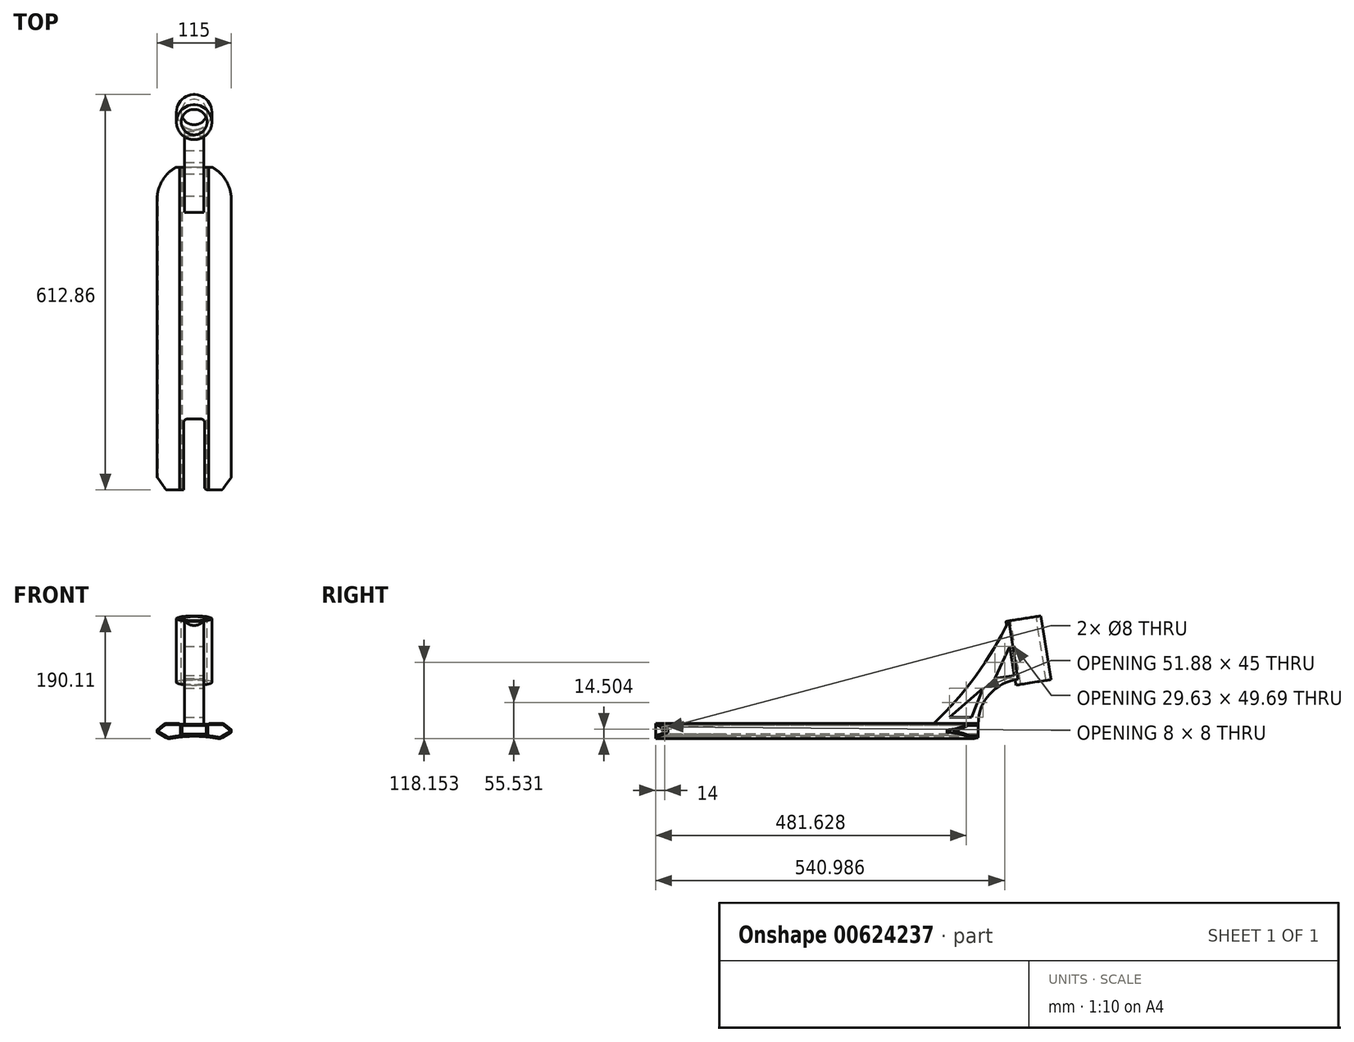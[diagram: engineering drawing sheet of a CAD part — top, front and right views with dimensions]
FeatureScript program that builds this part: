
annotation { "Feature Type Name" : "Feature", "Feature Type Description" : "" }
export const myFeature = defineFeature(function(context is Context, id is Id, definition is map)
    precondition{}
    {
        {
            var Q0;
            Q0=qCreatedBy(makeId("Front.planeOp"),FACE);
            var sketch = newSketch(context, id + "F0", { "sketchPlane" : qUnion([Q0])});
            skLineSegment(sketch, "E0", {"start": v(0, 0) * mm, "end": v(0, 27.74) * mm, "construction": true});
            skLineSegment(sketch, "E1", {"start": v(0, 23.15) * mm, "end": v(22.5, 23.15) * mm});
            skLineSegment(sketch, "E2", {"start": v(22.5, 23.15) * mm, "end": v(22.5, 24.45) * mm});
            skLineSegment(sketch, "E3", {"start": v(22.5, 24.45) * mm, "end": v(45.58, 24.45) * mm});
            skLineSegment(sketch, "E4", {"start": v(45.58, 24.45) * mm, "end": v(57.5, 14.45) * mm});
            skLineSegment(sketch, "E5", {"start": v(57.5, 14.45) * mm, "end": v(57.5, 10.45) * mm});
            skLineSegment(sketch, "E6", {"start": v(57.5, 10.45) * mm, "end": v(40.18, 0.45) * mm});
            skLineSegment(sketch, "E7.MirrorCS", {"start": v(0, 23.15) * mm, "end": v(-22.5, 23.15) * mm});
            skLineSegment(sketch, "E8.MirrorCS", {"start": v(-22.5, 23.15) * mm, "end": v(-22.5, 24.45) * mm});
            skLineSegment(sketch, "E9.MirrorCS", {"start": v(-22.5, 24.45) * mm, "end": v(-45.58, 24.45) * mm});
            skLineSegment(sketch, "E10.MirrorCS", {"start": v(-45.58, 24.45) * mm, "end": v(-57.5, 14.45) * mm});
            skLineSegment(sketch, "E11.MirrorCS", {"start": v(-57.5, 14.45) * mm, "end": v(-57.5, 10.45) * mm});
            skLineSegment(sketch, "E12.MirrorCS", {"start": v(-57.5, 10.45) * mm, "end": v(-40.18, 0.45) * mm});
            skArc(sketch, "E13", {"start": v(40.18, 0.45) * mm, "mid": v(0, 4.53) * mm, "end": v(-40.18, 0.45) * mm});
            skSolve(sketch);
        }
        {
            var Q0;
            Q0=qSketchRegion(id+"F0",true);
            extrude(context, id + "F1", {"entities" : qUnion([Q0]), "endBound" : BoundingType.SYMMETRIC, "depth" : 500 * mm});
        }
        {
            var Q0;
            Q0=qCreatedBy(makeId("Front.planeOp"),FACE);
            var sketch = newSketch(context, id + "F2", { "sketchPlane" : qUnion([Q0])});
            skLineSegment(sketch, "E14.bottom", {"start": v(-19, 21.15) * mm, "end": v(19, 21.15) * mm});
            skLineSegment(sketch, "E14.top", {"start": v(-19, 8.15) * mm, "end": v(19, 8.15) * mm});
            skLineSegment(sketch, "E14.left", {"start": v(-19, 21.15) * mm, "end": v(-19, 8.15) * mm});
            skLineSegment(sketch, "E14.right", {"start": v(19, 21.15) * mm, "end": v(19, 8.15) * mm});
            skSolve(sketch);
        }
        {
            var Q0;
            Q0=qSketchRegion(id+"F2",true);
            extrude(context, id + "F3", {"entities" : qUnion([Q0]), "operationType" : NewBodyOperationType.REMOVE, "endBound" : BoundingType.SYMMETRIC, "oppositeDirection" : true, "depth" : 500 * mm});
        }
        {
            var Q0;
            Q0=makeQuery(id+"F1.opExtrude","SWEPT_EDGE",EDGE,{"disambiguationData":[OSD([sQuery(id+"F0.wireOp",EDGE,"E8.MirrorCS"),sQuery(id+"F0.wireOp",EDGE,"E9.MirrorCS")])]});
            var Q1;
            Q1=makeQuery(id+"F1.opExtrude","SWEPT_EDGE",EDGE,{"disambiguationData":[OSD([sQuery(id+"F0.wireOp",EDGE,"E2"),sQuery(id+"F0.wireOp",EDGE,"E3")])]});
            fillet(context, id + "F4", {"entities" : qUnion([Q0, Q1]), "radius" : 2 * mm, "tangentPropagation" : true, "allowEdgeOverflow" : false});
        }
        {
            var Q0;
            Q0=makeQuery(id+"F1.opExtrude","SWEPT_EDGE",EDGE,{"disambiguationData":[OSD([sQuery(id+"F0.wireOp",EDGE,"E9.MirrorCS"),sQuery(id+"F0.wireOp",EDGE,"E10.MirrorCS")])]});
            var Q1;
            Q1=makeQuery(id+"F1.opExtrude","SWEPT_EDGE",EDGE,{"disambiguationData":[OSD([sQuery(id+"F0.wireOp",EDGE,"E12.MirrorCS"),sQuery(id+"F0.wireOp",EDGE,"E13")])]});
            var Q2;
            Q2=makeQuery(id+"F1.opExtrude","SWEPT_EDGE",EDGE,{"disambiguationData":[OSD([sQuery(id+"F0.wireOp",EDGE,"E6"),sQuery(id+"F0.wireOp",EDGE,"E13")])]});
            var Q3;
            Q3=makeQuery(id+"F1.opExtrude","SWEPT_EDGE",EDGE,{"disambiguationData":[OSD([sQuery(id+"F0.wireOp",EDGE,"E3"),sQuery(id+"F0.wireOp",EDGE,"E4")])]});
            fillet(context, id + "F5", {"entities" : qUnion([Q0, Q1, Q2, Q3]), "radius" : 9 * mm, "tangentPropagation" : true, "allowEdgeOverflow" : false});
        }
        {
            var Q0;
            Q0=makeQuery(id+"F1.opExtrude","SWEPT_EDGE",EDGE,{"disambiguationData":[OSD([sQuery(id+"F0.wireOp",EDGE,"E4"),sQuery(id+"F0.wireOp",EDGE,"E5")])]});
            var Q1;
            Q1=makeQuery(id+"F1.opExtrude","SWEPT_EDGE",EDGE,{"disambiguationData":[OSD([sQuery(id+"F0.wireOp",EDGE,"E5"),sQuery(id+"F0.wireOp",EDGE,"E6")])]});
            var Q2;
            Q2=makeQuery(id+"F1.opExtrude","SWEPT_EDGE",EDGE,{"disambiguationData":[OSD([sQuery(id+"F0.wireOp",EDGE,"E11.MirrorCS"),sQuery(id+"F0.wireOp",EDGE,"E12.MirrorCS")])]});
            var Q3;
            Q3=makeQuery(id+"F1.opExtrude","SWEPT_EDGE",EDGE,{"disambiguationData":[OSD([sQuery(id+"F0.wireOp",EDGE,"E10.MirrorCS"),sQuery(id+"F0.wireOp",EDGE,"E11.MirrorCS")])]});
            fillet(context, id + "F6", {"entities" : qUnion([Q0, Q1, Q2, Q3]), "radius" : 1 * mm, "tangentPropagation" : true, "allowEdgeOverflow" : false});
        }
        {
            var Q0;
            Q0=makeQuery(id+"F1.opExtrude","CAP_FACE",FACE,{"disambiguationData":[OSD([sQuery(id+"F0.wireOp",EDGE,"E1"),sQuery(id+"F0.wireOp",EDGE,"E2"),sQuery(id+"F0.wireOp",EDGE,"E3"),sQuery(id+"F0.wireOp",EDGE,"E4"),sQuery(id+"F0.wireOp",EDGE,"E5"),sQuery(id+"F0.wireOp",EDGE,"E6"),sQuery(id+"F0.wireOp",EDGE,"E7.MirrorCS"),sQuery(id+"F0.wireOp",EDGE,"E8.MirrorCS"),sQuery(id+"F0.wireOp",EDGE,"E9.MirrorCS"),sQuery(id+"F0.wireOp",EDGE,"E10.MirrorCS"),sQuery(id+"F0.wireOp",EDGE,"E11.MirrorCS"),sQuery(id+"F0.wireOp",EDGE,"E12.MirrorCS"),sQuery(id+"F0.wireOp",EDGE,"E13")])],"isStart":false});
            var sketch = newSketch(context, id + "F7", { "sketchPlane" : qUnion([Q0])});
            skLineSegment(sketch, "E15.0.0", {"start": v(43.1, 2.14) * mm, "end": v(57, 10.16) * mm});
            skArc(sketch, "E15.0.1", {"start": v(57, 10.16) * mm, "mid": v(57.37, 10.53) * mm, "end": v(57.5, 11.03) * mm});
            skLineSegment(sketch, "E15.0.2", {"start": v(57.5, 11.03) * mm, "end": v(57.5, 13.99) * mm});
            skArc(sketch, "E15.0.3", {"start": v(57.5, 13.99) * mm, "mid": v(57.4, 14.4) * mm, "end": v(57.14, 14.75) * mm});
            skLineSegment(sketch, "E15.0.4", {"start": v(57.14, 14.75) * mm, "end": v(48.1, 22.35) * mm});
            skArc(sketch, "E15.0.5", {"start": v(48.1, 22.35) * mm, "mid": v(45.38, 23.9) * mm, "end": v(42.3, 24.45) * mm});
            skLineSegment(sketch, "E15.0.6", {"start": v(42.3, 24.45) * mm, "end": v(24.37, 24.45) * mm});
            skArc(sketch, "E15.0.7", {"start": v(24.37, 24.45) * mm, "mid": v(23.23, 24.1) * mm, "end": v(22.5, 23.15) * mm});
            skLineSegment(sketch, "E15.0.8", {"start": v(22.5, 23.15) * mm, "end": v(-22.5, 23.15) * mm});
            skArc(sketch, "E15.0.9", {"start": v(-22.5, 23.15) * mm, "mid": v(-23.23, 24.1) * mm, "end": v(-24.37, 24.45) * mm});
            skLineSegment(sketch, "E15.0.10", {"start": v(-24.37, 24.45) * mm, "end": v(-42.3, 24.45) * mm});
            skArc(sketch, "E15.0.11", {"start": v(-42.3, 24.45) * mm, "mid": v(-45.38, 23.9) * mm, "end": v(-48.1, 22.35) * mm});
            skLineSegment(sketch, "E15.0.12", {"start": v(-48.1, 22.35) * mm, "end": v(-57.14, 14.75) * mm});
            skArc(sketch, "E15.0.13", {"start": v(-57.14, 14.75) * mm, "mid": v(-57.4, 14.4) * mm, "end": v(-57.5, 13.99) * mm});
            skLineSegment(sketch, "E15.0.14", {"start": v(-57.5, 13.99) * mm, "end": v(-57.5, 11.03) * mm});
            skArc(sketch, "E15.0.15", {"start": v(-57.5, 11.03) * mm, "mid": v(-57.37, 10.53) * mm, "end": v(-57, 10.16) * mm});
            skLineSegment(sketch, "E15.0.16", {"start": v(-57, 10.16) * mm, "end": v(-43.1, 2.14) * mm});
            skArc(sketch, "E15.0.17", {"start": v(-43.1, 2.14) * mm, "mid": v(-40.12, 1.06) * mm, "end": v(-36.94, 1.09) * mm});
            skArc(sketch, "E15.0.18", {"start": v(-36.94, 1.09) * mm, "mid": v(0, 4.53) * mm, "end": v(36.94, 1.09) * mm});
            skArc(sketch, "E15.0.19", {"start": v(36.94, 1.09) * mm, "mid": v(40.12, 1.06) * mm, "end": v(43.1, 2.14) * mm});
            skArc(sketch, "E16.0", {"start": v(-37.3, 3.05) * mm, "mid": v(0, 6.53) * mm, "end": v(37.3, 3.05) * mm});
            skArc(sketch, "E16.1", {"start": v(-42.1, 3.87) * mm, "mid": v(-39.78, 3.03) * mm, "end": v(-37.3, 3.05) * mm});
            skLineSegment(sketch, "E16.2", {"start": v(-24.37, 22.45) * mm, "end": v(-42.3, 22.45) * mm});
            skArc(sketch, "E16.3", {"start": v(-42.3, 22.45) * mm, "mid": v(-44.7, 22.03) * mm, "end": v(-46.8, 20.81) * mm});
            skLineSegment(sketch, "E16.4", {"start": v(-46.8, 20.81) * mm, "end": v(-55.76, 13.3) * mm});
            skLineSegment(sketch, "E16.5", {"start": v(-55.61, 11.67) * mm, "end": v(-42.1, 3.87) * mm});
            skPoint(sketch, "E17.visualSharp", {"position": v(-56.85, 12.39) * mm});
            skArc(sketch, "E17.filletArc", {"start": v(-55.76, 13.3) * mm, "mid": v(-56.1, 12.45) * mm, "end": v(-55.61, 11.67) * mm});
            skLineSegment(sketch, "E18", {"start": v(-21, 5.43) * mm, "end": v(-21, 21.15) * mm});
            skLineSegment(sketch, "E19", {"start": v(-21, 21.15) * mm, "end": v(-22.5, 21.15) * mm});
            skArc(sketch, "E20", {"start": v(-22.5, 21.15) * mm, "mid": v(-23.23, 22.1) * mm, "end": v(-24.37, 22.45) * mm});
            skLineSegment(sketch, "E21.MirrorCS", {"start": v(21, 5.43) * mm, "end": v(21, 21.15) * mm});
            skLineSegment(sketch, "E22.MirrorCS", {"start": v(21, 21.15) * mm, "end": v(22.5, 21.15) * mm});
            skArc(sketch, "E23.MirrorCS", {"start": v(22.5, 21.15) * mm, "mid": v(23.23, 22.1) * mm, "end": v(24.37, 22.45) * mm});
            skLineSegment(sketch, "E24.MirrorCS", {"start": v(24.37, 22.45) * mm, "end": v(42.3, 22.45) * mm});
            skArc(sketch, "E25.MirrorCS", {"start": v(42.3, 22.45) * mm, "mid": v(44.7, 22.03) * mm, "end": v(46.8, 20.81) * mm});
            skLineSegment(sketch, "E26.MirrorCS", {"start": v(46.8, 20.81) * mm, "end": v(55.76, 13.3) * mm});
            skArc(sketch, "E27.MirrorCS", {"start": v(55.76, 13.3) * mm, "mid": v(56.1, 12.45) * mm, "end": v(55.61, 11.67) * mm});
            skLineSegment(sketch, "E28.MirrorCS", {"start": v(55.61, 11.67) * mm, "end": v(42.1, 3.87) * mm});
            skArc(sketch, "E29.MirrorCS", {"start": v(42.1, 3.87) * mm, "mid": v(39.78, 3.03) * mm, "end": v(37.3, 3.05) * mm});
            skArc(sketch, "E30.MirrorCS", {"start": v(37.3, 3.05) * mm, "mid": v(0, 6.53) * mm, "end": v(-37.3, 3.05) * mm});
            skSolve(sketch);
        }
        {
            var Q0;
            {var subQ0=sQuery(id+"F7.wireOp",EDGE,"E16.1");Q0=makeQuery(id+"F7.imprint","IMPRINT",FACE,{"disambiguationData":[TD([[makeQuery(id+"F7.imprint","IMPRINT",EDGE,{"derivedFrom":subQ0}),1.0]])]});}
            var Q1;
            {var subQ0=sQuery(id+"F7.wireOp",EDGE,"E21.MirrorCS");Q1=makeQuery(id+"F7.imprint","IMPRINT",FACE,{"disambiguationData":[TD([[makeQuery(id+"F7.imprint","IMPRINT",EDGE,{"derivedFrom":subQ0}),-1.0]])]});}
            extrude(context, id + "F8", {"entities" : qUnion([Q0, Q1]), "operationType" : NewBodyOperationType.REMOVE, "endBound" : BoundingType.THROUGH_ALL, "oppositeDirection" : true, "depth" : 25 * mm});
        }
        {
            var Q0;
            Q0=qCreatedBy(makeId("Top.planeOp"),FACE);
            var sketch = newSketch(context, id + "F9", { "sketchPlane" : qUnion([Q0])});
            skArc(sketch, "E31", {"start": v(57.5, 200) * mm, "mid": v(0, 257.5) * mm, "end": v(-57.5, 200) * mm});
            skLineSegment(sketch, "E32", {"start": v(57.5, 200) * mm, "end": v(57.5, 280) * mm});
            skLineSegment(sketch, "E33", {"start": v(57.5, 280) * mm, "end": v(-57.5, 280) * mm});
            skLineSegment(sketch, "E34", {"start": v(-57.5, 280) * mm, "end": v(-57.5, 200) * mm});
            skSolve(sketch);
        }
        {
            var Q0;
            Q0=qSketchRegion(id+"F9",true);
            extrude(context, id + "F10", {"entities" : qUnion([Q0]), "operationType" : NewBodyOperationType.REMOVE, "endBound" : BoundingType.THROUGH_ALL, "depth" : 25 * mm, "hasSecondDirection" : true, "secondDirectionBound" : SecondDirectionBoundingType.THROUGH_ALL, "secondDirectionOppositeDirection" : true, "secondDirectionDepth" : 25 * mm});
        }
        {
            var Q0;
            Q0=qCreatedBy(makeId("Top.planeOp"),FACE);
            var sketch = newSketch(context, id + "F11", { "sketchPlane" : qUnion([Q0])});
            skLineSegment(sketch, "E35", {"start": v(-68, -216) * mm, "end": v(-43.3, -250) * mm});
            skLineSegment(sketch, "E36", {"start": v(-68, -216) * mm, "end": v(-68, -346) * mm});
            skLineSegment(sketch, "E37", {"start": v(-68, -346) * mm, "end": v(68, -346) * mm});
            skLineSegment(sketch, "E38", {"start": v(68, -346) * mm, "end": v(68, -216) * mm});
            skLineSegment(sketch, "E39", {"start": v(68, -216) * mm, "end": v(43.3, -250) * mm});
            skLineSegment(sketch, "E40", {"start": v(-43.3, -250) * mm, "end": v(-16, -250) * mm});
            skLineSegment(sketch, "E41", {"start": v(-16, -250) * mm, "end": v(-16, -140) * mm});
            skLineSegment(sketch, "E42", {"start": v(-16, -140) * mm, "end": v(16, -140) * mm});
            skLineSegment(sketch, "E43", {"start": v(16, -140) * mm, "end": v(16, -250) * mm});
            skLineSegment(sketch, "E44", {"start": v(16, -250) * mm, "end": v(43.3, -250) * mm});
            skSolve(sketch);
        }
        {
            var Q0;
            Q0=qSketchRegion(id+"F11",true);
            extrude(context, id + "F12", {"entities" : qUnion([Q0]), "operationType" : NewBodyOperationType.REMOVE, "endBound" : BoundingType.THROUGH_ALL, "oppositeDirection" : true, "depth" : 25 * mm, "hasSecondDirection" : true, "secondDirectionBound" : SecondDirectionBoundingType.THROUGH_ALL, "secondDirectionOppositeDirection" : false, "secondDirectionDepth" : 25 * mm});
        }
        {
            var Q0;
            {var subQ2=sQuery(id+"F11.wireOp",EDGE,"E43");Q0=makeQuery(id+"F12.boolean.opBoolean","COPY",EDGE,{"disambiguationData":[TD([makeQuery(id+"F3.boolean.opBoolean","COPY",FACE,{"derivedFrom":makeQuery(id+"F3.opExtrude","SWEPT_FACE",FACE,{"disambiguationData":[OSD([sQuery(id+"F2.wireOp",EDGE,"E14.bottom")])]})})])],"derivedFrom":makeQuery(id+"F12.opExtrude","SWEPT_EDGE",EDGE,{"disambiguationData":[OSD([subQ2,sQuery(id+"F11.wireOp",EDGE,"E44")])]})});}
            var Q1;
            {var subQ0=sQuery(id+"F0.wireOp",EDGE,"E13");var subQ1=sQuery(id+"F11.wireOp",EDGE,"E43");Q1=makeQuery(id+"F12.boolean.opBoolean","COPY",EDGE,{"disambiguationData":[TD([makeQuery(id+"F1.opExtrude","SWEPT_FACE",FACE,{"disambiguationData":[OSD([subQ0])]})])],"derivedFrom":makeQuery(id+"F12.opExtrude","SWEPT_EDGE",EDGE,{"disambiguationData":[OSD([subQ1,sQuery(id+"F11.wireOp",EDGE,"E44")])]})});}
            var Q2;
            {var subQ0=sQuery(id+"F11.wireOp",EDGE,"E42");var subQ1=sQuery(id+"F11.wireOp",EDGE,"E43");Q2=makeQuery(id+"F12.boolean.opBoolean","COPY",EDGE,{"disambiguationData":[TD([makeQuery(id+"F3.boolean.opBoolean","COPY",FACE,{"derivedFrom":makeQuery(id+"F3.opExtrude","SWEPT_FACE",FACE,{"disambiguationData":[OSD([sQuery(id+"F2.wireOp",EDGE,"E14.bottom")])]})})])],"derivedFrom":makeQuery(id+"F12.opExtrude","SWEPT_EDGE",EDGE,{"disambiguationData":[OSD([subQ0,subQ1])]})});}
            var Q3;
            {var subQ0=sQuery(id+"F11.wireOp",EDGE,"E43");var subQ1=sQuery(id+"F11.wireOp",EDGE,"E42");Q3=makeQuery(id+"F12.boolean.opBoolean","COPY",EDGE,{"disambiguationData":[TD([makeQuery(id+"F1.opExtrude","SWEPT_FACE",FACE,{"disambiguationData":[OSD([sQuery(id+"F0.wireOp",EDGE,"E13")])]})])],"derivedFrom":makeQuery(id+"F12.opExtrude","SWEPT_EDGE",EDGE,{"disambiguationData":[OSD([subQ1,subQ0])]})});}
            var Q4;
            {var subQ0=sQuery(id+"F11.wireOp",EDGE,"E42");var subQ1=sQuery(id+"F11.wireOp",EDGE,"E41");Q4=makeQuery(id+"F12.boolean.opBoolean","COPY",EDGE,{"disambiguationData":[TD([makeQuery(id+"F3.boolean.opBoolean","COPY",FACE,{"derivedFrom":makeQuery(id+"F3.opExtrude","SWEPT_FACE",FACE,{"disambiguationData":[OSD([sQuery(id+"F2.wireOp",EDGE,"E14.bottom")])]})})])],"derivedFrom":makeQuery(id+"F12.opExtrude","SWEPT_EDGE",EDGE,{"disambiguationData":[OSD([subQ1,subQ0])]})});}
            var Q5;
            {var subQ0=sQuery(id+"F11.wireOp",EDGE,"E41");var subQ1=sQuery(id+"F11.wireOp",EDGE,"E42");Q5=makeQuery(id+"F12.boolean.opBoolean","COPY",EDGE,{"disambiguationData":[TD([makeQuery(id+"F1.opExtrude","SWEPT_FACE",FACE,{"disambiguationData":[OSD([sQuery(id+"F0.wireOp",EDGE,"E13")])]})])],"derivedFrom":makeQuery(id+"F12.opExtrude","SWEPT_EDGE",EDGE,{"disambiguationData":[OSD([subQ0,subQ1])]})});}
            var Q6;
            {var subQ2=sQuery(id+"F11.wireOp",EDGE,"E41");Q6=makeQuery(id+"F12.boolean.opBoolean","COPY",EDGE,{"disambiguationData":[TD([makeQuery(id+"F3.boolean.opBoolean","COPY",FACE,{"derivedFrom":makeQuery(id+"F3.opExtrude","SWEPT_FACE",FACE,{"disambiguationData":[OSD([sQuery(id+"F2.wireOp",EDGE,"E14.bottom")])]})})])],"derivedFrom":makeQuery(id+"F12.opExtrude","SWEPT_EDGE",EDGE,{"disambiguationData":[OSD([sQuery(id+"F11.wireOp",EDGE,"E40"),subQ2])]})});}
            var Q7;
            {var subQ0=sQuery(id+"F0.wireOp",EDGE,"E13");var subQ1=sQuery(id+"F11.wireOp",EDGE,"E41");Q7=makeQuery(id+"F12.boolean.opBoolean","COPY",EDGE,{"disambiguationData":[TD([makeQuery(id+"F1.opExtrude","SWEPT_FACE",FACE,{"disambiguationData":[OSD([subQ0])]})])],"derivedFrom":makeQuery(id+"F12.opExtrude","SWEPT_EDGE",EDGE,{"disambiguationData":[OSD([sQuery(id+"F11.wireOp",EDGE,"E40"),subQ1])]})});}
            fillet(context, id + "F13", {"entities" : qUnion([Q0, Q1, Q2, Q3, Q4, Q5, Q6, Q7]), "radius" : 5 * mm, "tangentPropagation" : true, "allowEdgeOverflow" : false});
        }
        {
            var Q0;
            Q0=qCreatedBy(makeId("Right.planeOp"),FACE);
            var sketch = newSketch(context, id + "F14", { "sketchPlane" : qUnion([Q0])});
            skLineSegment(sketch, "E45", {"start": v(180, 23.15) * mm, "end": v(250, 23.15) * mm});
            skArc(sketch, "E46", {"start": v(311.71, 92.66) * mm, "mid": v(267.66, 69.63) * mm, "end": v(250, 23.15) * mm});
            skLineSegment(sketch, "E47", {"start": v(313.03, 84.38) * mm, "end": v(358.46, 91.58) * mm});
            skLineSegment(sketch, "E48", {"start": v(358.46, 91.58) * mm, "end": v(342.82, 190.35) * mm});
            skLineSegment(sketch, "E49", {"start": v(342.82, 190.35) * mm, "end": v(297.38, 183.15) * mm});
            skArc(sketch, "E50", {"start": v(180, 23.15) * mm, "mid": v(245.97, 97.81) * mm, "end": v(297.38, 183.15) * mm});
            skLineSegment(sketch, "E51", {"start": v(311.71, 92.66) * mm, "end": v(313.03, 84.38) * mm});
            skSolve(sketch);
        }
        {
            var Q0;
            Q0=qSketchRegion(id+"F14",true);
            extrude(context, id + "F15", {"entities" : qUnion([Q0]), "operationType" : NewBodyOperationType.ADD, "endBound" : BoundingType.SYMMETRIC, "depth" : 30 * mm});
        }
        {
            var Q0;
            Q0=makeQuery(id+"F15.opExtrude","SWEPT_FACE",FACE,{"disambiguationData":[OSD([sQuery(id+"F14.wireOp",EDGE,"E49")])]});
            var sketch = newSketch(context, id + "F16", { "sketchPlane" : qUnion([Q0])});
            skCircle(sketch, "E52", {"center": v(0, 345.37) * mm, "radius": 27.46 * mm});
            skSolve(sketch);
        }
        {
            var Q0;
            Q0=qSketchRegion(id+"F16",true);
            var Q1;
            Q1=makeQuery(id+"F15.opExtrude","SWEPT_FACE",FACE,{"disambiguationData":[OSD([sQuery(id+"F14.wireOp",EDGE,"E47")])]});
            extrude(context, id + "F17", {"entities" : qUnion([Q0]), "operationType" : NewBodyOperationType.ADD, "endBound" : BoundingType.UP_TO_SURFACE, "oppositeDirection" : true, "endBoundEntityFace" : qUnion([Q1]), "depth" : 25 * mm});
        }
        {
            var Q0;
            Q0=makeQuery(id+"F17.boolean.opBoolean","MERGE",FACE,{"derivedFrom":[makeQuery(id+"F15.opExtrude","SWEPT_FACE",FACE,{"disambiguationData":[OSD([sQuery(id+"F14.wireOp",EDGE,"E49")])]}),makeQuery(id+"F17.opExtrude","CAP_FACE",FACE,{"disambiguationData":[OSD([sQuery(id+"F16.wireOp",EDGE,"E52")])],"isStart":true})]});
            var sketch = newSketch(context, id + "F18", { "sketchPlane" : qUnion([Q0])});
            skPoint(sketch, "E53", {"position": v(0, 345.37) * mm});
            skSolve(sketch);
        }
        {
            var Q0;
            Q0=sQuery(id+"F18.wireOp",VERTEX,"E53");
            var Q1;
            Q1=makeQuery(id+"F1.opExtrude","SWEPT_BODY",BODY,{"disambiguationData":[OSD([sQuery(id+"F0.wireOp",EDGE,"E1"),sQuery(id+"F0.wireOp",EDGE,"E2"),sQuery(id+"F0.wireOp",EDGE,"E3"),sQuery(id+"F0.wireOp",EDGE,"E4"),sQuery(id+"F0.wireOp",EDGE,"E5"),sQuery(id+"F0.wireOp",EDGE,"E6"),sQuery(id+"F0.wireOp",EDGE,"E7.MirrorCS"),sQuery(id+"F0.wireOp",EDGE,"E8.MirrorCS"),sQuery(id+"F0.wireOp",EDGE,"E9.MirrorCS"),sQuery(id+"F0.wireOp",EDGE,"E10.MirrorCS"),sQuery(id+"F0.wireOp",EDGE,"E11.MirrorCS"),sQuery(id+"F0.wireOp",EDGE,"E12.MirrorCS"),sQuery(id+"F0.wireOp",EDGE,"E13")])]});
            hole(context, id + "F19", {"style" : HoleStyle.SIMPLE, "endStyle" : HoleEndStyle.THROUGH, "holeDiameter" : 40 * mm, "isTappedThrough" : true, "tappedDepth" : 12 * mm, "tapClearance" : 3, "locations" : qUnion([Q0]), "scope" : qUnion([Q1])});
        }
        {
            var Q0;
            Q0=makeQuery(id+"F8.boolean.opBoolean","COPY",FACE,{"derivedFrom":makeQuery(id+"F8.opExtrude","SWEPT_FACE",FACE,{"disambiguationData":[OSD([sQuery(id+"F7.wireOp",EDGE,"E21.MirrorCS")])]})});
            var sketch = newSketch(context, id + "F20", { "sketchPlane" : qUnion([Q0])});
            skPoint(sketch, "E54", {"position": v(-236, 15.43) * mm});
            skSolve(sketch);
        }
        {
            var Q0;
            Q0=sQuery(id+"F20.wireOp",VERTEX,"E54");
            var Q1;
            Q1=makeQuery(id+"F1.opExtrude","SWEPT_BODY",BODY,{"disambiguationData":[OSD([sQuery(id+"F0.wireOp",EDGE,"E1"),sQuery(id+"F0.wireOp",EDGE,"E2"),sQuery(id+"F0.wireOp",EDGE,"E3"),sQuery(id+"F0.wireOp",EDGE,"E4"),sQuery(id+"F0.wireOp",EDGE,"E5"),sQuery(id+"F0.wireOp",EDGE,"E6"),sQuery(id+"F0.wireOp",EDGE,"E7.MirrorCS"),sQuery(id+"F0.wireOp",EDGE,"E8.MirrorCS"),sQuery(id+"F0.wireOp",EDGE,"E9.MirrorCS"),sQuery(id+"F0.wireOp",EDGE,"E10.MirrorCS"),sQuery(id+"F0.wireOp",EDGE,"E11.MirrorCS"),sQuery(id+"F0.wireOp",EDGE,"E12.MirrorCS"),sQuery(id+"F0.wireOp",EDGE,"E13")])]});
            hole(context, id + "F21", {"style" : HoleStyle.SIMPLE, "endStyle" : HoleEndStyle.BLIND, "holeDiameter" : 8 * mm, "holeDepth" : 50 * mm, "isTappedThrough" : true, "tappedDepth" : 12 * mm, "tapClearance" : 3, "locations" : qUnion([Q0]), "scope" : qUnion([Q1])});
        }
        {
            var Q0;
            Q0=makeQuery(id+"F15.opExtrude","CAP_FACE",FACE,{"disambiguationData":[OSD([sQuery(id+"F14.wireOp",EDGE,"E45"),sQuery(id+"F14.wireOp",EDGE,"E46"),sQuery(id+"F14.wireOp",EDGE,"E47"),sQuery(id+"F14.wireOp",EDGE,"E48"),sQuery(id+"F14.wireOp",EDGE,"E49"),sQuery(id+"F14.wireOp",EDGE,"E50"),sQuery(id+"F14.wireOp",EDGE,"E51")])],"isStart":false});
            var sketch = newSketch(context, id + "F22", { "sketchPlane" : qUnion([Q0])});
            skLineSegment(sketch, "E55", {"start": v(239.69, 33.96) * mm, "end": v(257.57, 78.96) * mm});
            skLineSegment(sketch, "E56", {"start": v(257.57, 78.96) * mm, "end": v(205.69, 34.21) * mm});
            skLineSegment(sketch, "E57", {"start": v(205.69, 34.21) * mm, "end": v(239.69, 33.96) * mm});
            skLineSegment(sketch, "E58", {"start": v(298.67, 143.93) * mm, "end": v(305.8, 98.93) * mm});
            skLineSegment(sketch, "E59", {"start": v(305.8, 98.93) * mm, "end": v(276.17, 94.24) * mm});
            skLineSegment(sketch, "E60", {"start": v(276.17, 94.24) * mm, "end": v(298.67, 143.93) * mm});
            skSolve(sketch);
        }
        {
            var Q0;
            Q0=makeQuery(id+"F22.imprint","IMPRINT",FACE,{"disambiguationData":[TD([[makeQuery(id+"F22.imprint","IMPRINT",EDGE,{"derivedFrom":sQuery(id+"F22.wireOp",EDGE,"E55")}),1.0]])]});
            var Q1;
            Q1=makeQuery(id+"F22.imprint","IMPRINT",FACE,{"disambiguationData":[TD([[makeQuery(id+"F22.imprint","IMPRINT",EDGE,{"derivedFrom":sQuery(id+"F22.wireOp",EDGE,"E58")}),-1.0]])]});
            extrude(context, id + "F23", {"entities" : qUnion([Q0, Q1]), "operationType" : NewBodyOperationType.REMOVE, "endBound" : BoundingType.THROUGH_ALL, "oppositeDirection" : true, "depth" : 25 * mm, "offsetDistance" : 25 * mm});
        }
    });
